# Revit family: QF_WELBILT-CONVOTHERM_CMX ET 6.10 ES.201127121746
name_source: partatom
category: Specialty Equipment
revit_build: Autodesk Revit 2016 (Build: 20150220_1215(x64)
units: mm (PartAtom-declared; Revit-internal decimal feet)

## family parameters
Always vertical = Yes
Cut with Voids When Loaded = No
OmniClass Number = 23.40.40.14
OmniClass Title = Food Service Equipment
Part Type = Normal
Room Calculation Point = No
Round Connector Dimension = Use Diameter
Shared = No
Work Plane-Based = No

## types (1)
- CMXET-6-10-ES_400V/3Ph/50Hz
    Accessory = No
    Apparent Power = 11300 VA
    Cold Water Flow = 0.0 L/s
    Cold Water Size = 19 mm
    Cold Water Temperature Recommended = 0 °C
    Conn Conduit = No
    Cost = 0 $
    Cycle = 50 Hz
    Depth Actual = 797 mm  [stored 2.61483 ft]
    Description = COMBI OVEN CMX EASYTOUCH 6+1 SHELVES GN 1/1 - RIGHT HINGED DOOR - ELECTRIC INJECTION
    Electric power = 11300 W
    FL Amps = 16 A
    Height Actual = 673 mm  [stored 2.20801 ft]
    Indirect Waste Size = 51 mm
    Length Actual = 875 mm  [stored 2.87073 ft]
    Manufacturer = WELBILT-CONVOTHERM
    Max Overcurrent Protection = 0 A
    Min Ckt Ampacity = 0 A
    Model = CMX ET 6.10 ES
    Number of Poles = 3
    Phase = 3
    URL = www.convotherm.com
    Volts = 400 V
    Weight = 104.00 kg

note: [stored X ft] marks values corroborated as IEEE doubles in the binary element streams (Revit-internal decimal feet)

## geometry (parser evidence)
native form markers: Sweep x7
no freeform markers — native parametric forms only
